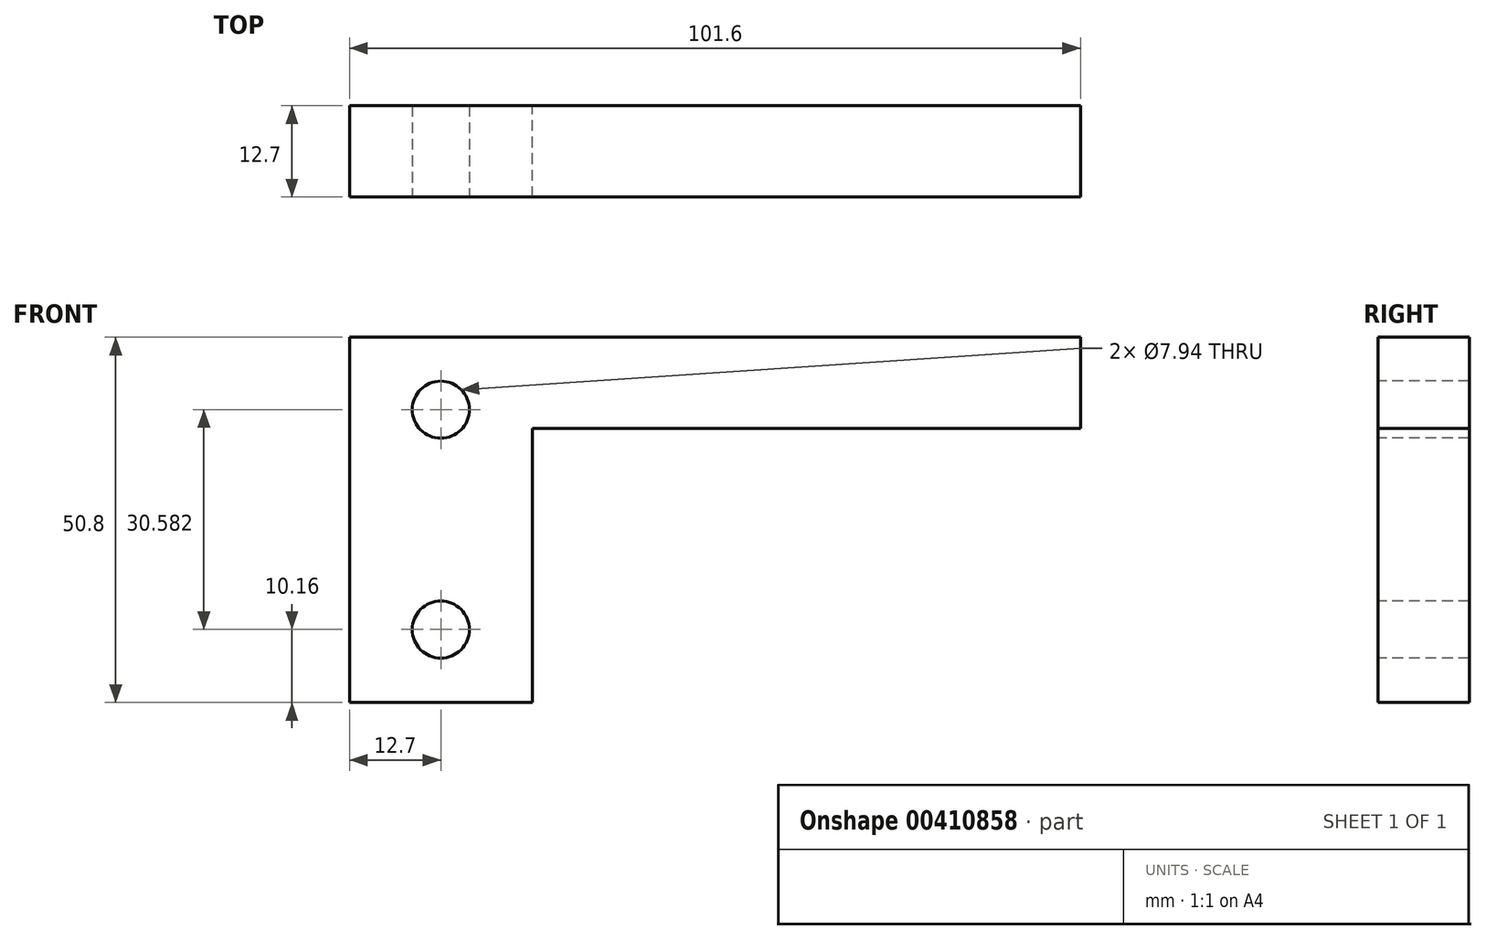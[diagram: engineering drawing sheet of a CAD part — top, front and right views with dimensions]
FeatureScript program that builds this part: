
annotation { "Feature Type Name" : "Feature", "Feature Type Description" : "" }
export const myFeature = defineFeature(function(context is Context, id is Id, definition is map)
    precondition{}
    {
        {
            var Q0;
            Q0=qCreatedBy(makeId("Front.planeOp"),FACE);
            var sketch = newSketch(context, id + "F0", { "sketchPlane" : qUnion([Q0])});
            skLineSegment(sketch, "E0", {"start": v(0, 0) * mm, "end": v(101.6, 0) * mm});
            skLineSegment(sketch, "E1", {"start": v(101.6, 0) * mm, "end": v(101.6, -12.7) * mm});
            skLineSegment(sketch, "E2", {"start": v(101.6, -12.7) * mm, "end": v(25.4, -12.7) * mm});
            skLineSegment(sketch, "E3", {"start": v(25.4, -12.7) * mm, "end": v(25.4, -50.8) * mm});
            skLineSegment(sketch, "E4", {"start": v(25.4, -50.8) * mm, "end": v(0, -50.8) * mm});
            skLineSegment(sketch, "E5", {"start": v(0, -50.8) * mm, "end": v(0, 0) * mm});
            skSolve(sketch);
        }
        {
            var Q0;
            Q0 = qSketchRegion(id + "F0", true);
            extrude(context, id + "F1", {"entities" : qUnion([Q0]), "depth" : 12.7 * mm});
        }
        {
            var Q0;
            Q0=makeQuery(id+"F1.opExtrude","CAP_FACE",FACE,{"disambiguationData":[OSD([sQuery(id+"F0.wireOp",EDGE,"E0"),sQuery(id+"F0.wireOp",EDGE,"E1"),sQuery(id+"F0.wireOp",EDGE,"E2"),sQuery(id+"F0.wireOp",EDGE,"E3"),sQuery(id+"F0.wireOp",EDGE,"E4"),sQuery(id+"F0.wireOp",EDGE,"E5")])],"isStart":false});
            var sketch = newSketch(context, id + "F2", { "sketchPlane" : qUnion([Q0])});
            skLineSegment(sketch, "E6", {"start": v(12.7, -10.06) * mm, "end": v(12.7, -40.64) * mm, "construction": true});
            skSolve(sketch);
        }
        {
            var Q0;
            Q0=sQuery(id+"F2.wireOp",VERTEX,"E6.start");
            var Q1;
            Q1=sQuery(id+"F2.wireOp",VERTEX,"E6.end");
            var Q2;
            Q2=makeQuery(id+"F1.opExtrude","SWEPT_BODY",BODY,{"disambiguationData":[OSD([sQuery(id+"F0.wireOp",EDGE,"E0"),sQuery(id+"F0.wireOp",EDGE,"E1"),sQuery(id+"F0.wireOp",EDGE,"E2"),sQuery(id+"F0.wireOp",EDGE,"E3"),sQuery(id+"F0.wireOp",EDGE,"E4"),sQuery(id+"F0.wireOp",EDGE,"E5")])]});
            hole(context, id + "F3", {"style" : HoleStyle.SIMPLE, "endStyle" : HoleEndStyle.THROUGH, "standardTappedOrClearance" : lookupTablePath({ "standard" : "ANSI", "engagement" : "75%", "pitch" : "16 tpi", "size" : "3/8", "type" : "Tapped" }), "standardBlindInLast" : lookupTablePath({ "standard" : "ANSI", "engagement" : "75%", "pitch" : "16 tpi", "size" : "3/8", "type" : "Tapped" }), "holeDiameter" : 7.94 * mm, "showTappedDepth" : true, "isTappedThrough" : true, "tappedDepth" : 12.7 * mm, "tapClearance" : 3, "locations" : qUnion([Q0, Q1]), "scope" : qUnion([Q2]), "majorDiameter" : 9.53 * mm});
        }
    });
